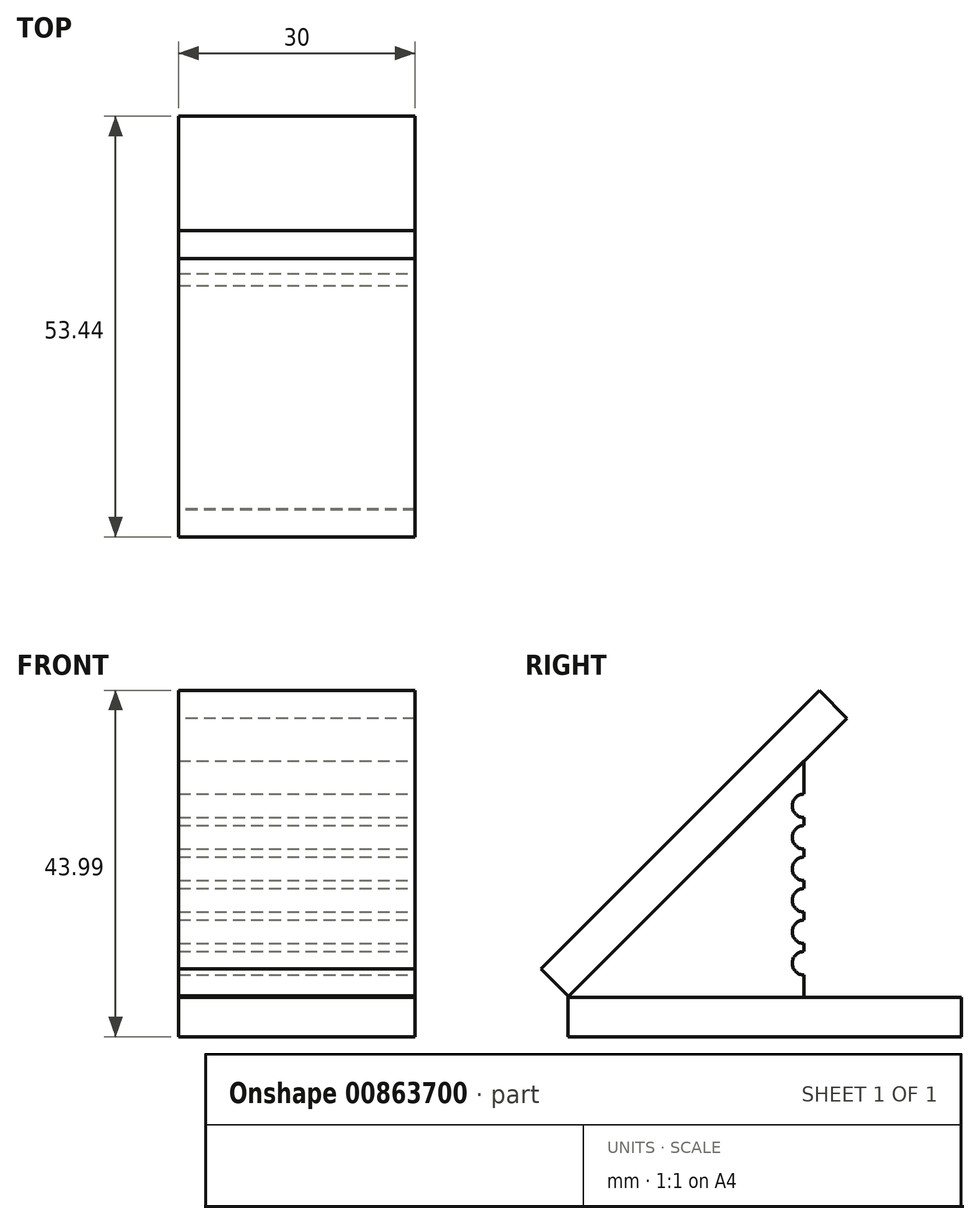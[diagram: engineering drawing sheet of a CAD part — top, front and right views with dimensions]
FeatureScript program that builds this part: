
annotation { "Feature Type Name" : "Feature", "Feature Type Description" : "" }
export const myFeature = defineFeature(function(context is Context, id is Id, definition is map)
    precondition{}
    {
        {
            var Q0;
            Q0=qCreatedBy(makeId("Top.planeOp"),FACE);
            var sketch = newSketch(context, id + "F0", { "sketchPlane" : qUnion([Q0])});
            skLineSegment(sketch, "E0.bottom", {"start": v(-15, 25) * mm, "end": v(15, 25) * mm});
            skLineSegment(sketch, "E0.top", {"start": v(-15, -25) * mm, "end": v(15, -25) * mm});
            skLineSegment(sketch, "E0.left", {"start": v(-15, 25) * mm, "end": v(-15, -25) * mm});
            skLineSegment(sketch, "E0.right", {"start": v(15, 25) * mm, "end": v(15, -25) * mm});
            skSolve(sketch);
        }
        {
            var Q0;
            Q0=makeQuery(id+"F0.imprint","IMPRINT",FACE,{"disambiguationData":[TD([[makeQuery(id+"F0.imprint","IMPRINT",EDGE,{"derivedFrom":sQuery(id+"F0.wireOp",EDGE,"E0.bottom")}),-1.0]])]});
            extrude(context, id + "F1", {"entities" : qUnion([Q0]), "depth" : 5 * mm, "offsetDistance" : 25 * mm});
        }
        {
            var Q0;
            Q0=makeQuery(id+"F1.opExtrude","CAP_EDGE",EDGE,{"disambiguationData":[OSD([sQuery(id+"F0.wireOp",EDGE,"E0.top")])],"isStart":false});
            cPlane(context, id + "F2", {"entities" : qUnion([Q0]), "cplaneType" : CPlaneType.LINE_ANGLE, "offset" : 25 * mm, "angle" : 45 * degree, "oppositeDirection" : true, "width" : 150 * mm, "height" : 150 * mm});
        }
        {
            var Q0;
            Q0=qCreatedBy(id+"F2.planeOp",FACE);
            var sketch = newSketch(context, id + "F3", { "sketchPlane" : qUnion([Q0])});
            skLineSegment(sketch, "E1.bottom", {"start": v(-15, -14) * mm, "end": v(15, -14) * mm});
            skLineSegment(sketch, "E1.top", {"start": v(-15, 36) * mm, "end": v(15, 36) * mm});
            skLineSegment(sketch, "E1.left", {"start": v(-15, -14) * mm, "end": v(-15, 36) * mm});
            skLineSegment(sketch, "E1.right", {"start": v(15, -14) * mm, "end": v(15, 36) * mm});
            skSolve(sketch);
        }
        {
            var Q0;
            Q0=makeQuery(id+"F3.imprint","IMPRINT",FACE,{"disambiguationData":[TD([[makeQuery(id+"F3.imprint","IMPRINT",EDGE,{"derivedFrom":sQuery(id+"F3.wireOp",EDGE,"E1.bottom")}),1.0]])]});
            extrude(context, id + "F4", {"entities" : qUnion([Q0]), "oppositeDirection" : true, "depth" : 5 * mm, "offsetDistance" : 25 * mm});
        }
        {
            var Q0;
            Q0=makeQuery(id+"F1.opExtrude","CAP_FACE",FACE,{"disambiguationData":[OSD([sQuery(id+"F0.wireOp",EDGE,"E0.bottom"),sQuery(id+"F0.wireOp",EDGE,"E0.top"),sQuery(id+"F0.wireOp",EDGE,"E0.left"),sQuery(id+"F0.wireOp",EDGE,"E0.right")])],"isStart":false});
            var sketch = newSketch(context, id + "F5", { "sketchPlane" : qUnion([Q0])});
            skLineSegment(sketch, "E2.top", {"start": v(15, 5) * mm, "end": v(-15, 5) * mm});
            skLineSegment(sketch, "E2.left", {"start": v(15, -25) * mm, "end": v(15, 5) * mm});
            skLineSegment(sketch, "E2.right", {"start": v(-15, -25) * mm, "end": v(-15, 5) * mm});
            skSolve(sketch);
        }
        {
            var Q0;
            Q0=makeQuery(id+"F5.imprint","IMPRINT",FACE,{"disambiguationData":[TD([[makeQuery(id+"F5.imprint","IMPRINT",EDGE,{"derivedFrom":sQuery(id+"F5.wireOp",EDGE,"E2.top")}),1.0]])]});
            extrude(context, id + "F6", {"entities" : qUnion([Q0]), "endBound" : BoundingType.UP_TO_NEXT, "depth" : 25 * mm, "offsetDistance" : 25 * mm});
        }
        {
            var Q0;
            Q0=makeQuery(id+"F6.opExtrude","SWEPT_FACE",FACE,{"disambiguationData":[OSD([sQuery(id+"F5.wireOp",EDGE,"E2.left")])]});
            var sketch = newSketch(context, id + "F7", { "sketchPlane" : qUnion([Q0])});
            skCircle(sketch, "E3", {"center": v(5, 29.32) * mm, "radius": 1.5 * mm});
            skCircle(sketch, "E4.0.1.0", {"center": v(5, 25.32) * mm, "radius": 1.5 * mm});
            skCircle(sketch, "E4.0.2.0", {"center": v(5, 21.32) * mm, "radius": 1.5 * mm});
            skCircle(sketch, "E4.0.3.0", {"center": v(5, 17.32) * mm, "radius": 1.5 * mm});
            skCircle(sketch, "E4.0.4.0", {"center": v(5, 13.32) * mm, "radius": 1.5 * mm});
            skLineSegment(sketch, "E4.direction1", {"start": v(5, 29.32) * mm, "end": v(-20, 29.32) * mm, "construction": true});
            skLineSegment(sketch, "E4.direction2", {"start": v(5, 29.32) * mm, "end": v(5, 25.32) * mm, "construction": true});
            skCircle(sketch, "E5.0.0.5", {"center": v(5, 9.32) * mm, "radius": 1.5 * mm});
            skSolve(sketch);
        }
        {
            var Q0;
            {var subQ0=sQuery(id+"F7.wireOp",EDGE,"E4.0.1.0");var subQ1=makeQuery(id+"F6.opExtrude","SWEPT_EDGE",EDGE,{"disambiguationData":[OSD([sQuery(id+"F0.wireOp",EDGE,"E0.right"),sQuery(id+"F5.wireOp",EDGE,"E2.top"),sQuery(id+"F5.wireOp",EDGE,"E2.left")])]});var subQ2=makeQuery(id+"F7.imprint","INTERSECT",VERTEX,{"disambiguationData":[OD(0.0)],"derivedFrom":[subQ1,subQ0]});Q0=makeQuery(id+"F7.imprint","IMPRINT",FACE,{"disambiguationData":[TD([[makeQuery(id+"F7.imprint","IMPRINT",EDGE,{"disambiguationData":[TD([[subQ2,-1.0]])],"derivedFrom":subQ0}),1.0]])]});}
            var Q1;
            {var subQ0=sQuery(id+"F7.wireOp",EDGE,"E4.0.2.0");var subQ1=makeQuery(id+"F6.opExtrude","SWEPT_EDGE",EDGE,{"disambiguationData":[OSD([sQuery(id+"F0.wireOp",EDGE,"E0.right"),sQuery(id+"F5.wireOp",EDGE,"E2.top"),sQuery(id+"F5.wireOp",EDGE,"E2.left")])]});var subQ2=makeQuery(id+"F7.imprint","INTERSECT",VERTEX,{"disambiguationData":[OD(0.0)],"derivedFrom":[subQ1,subQ0]});Q1=makeQuery(id+"F7.imprint","IMPRINT",FACE,{"disambiguationData":[TD([[makeQuery(id+"F7.imprint","IMPRINT",EDGE,{"disambiguationData":[TD([[subQ2,-1.0]])],"derivedFrom":subQ0}),1.0]])]});}
            var Q2;
            {var subQ0=sQuery(id+"F7.wireOp",EDGE,"E4.0.3.0");var subQ1=makeQuery(id+"F6.opExtrude","SWEPT_EDGE",EDGE,{"disambiguationData":[OSD([sQuery(id+"F0.wireOp",EDGE,"E0.right"),sQuery(id+"F5.wireOp",EDGE,"E2.top"),sQuery(id+"F5.wireOp",EDGE,"E2.left")])]});var subQ2=makeQuery(id+"F7.imprint","INTERSECT",VERTEX,{"disambiguationData":[OD(0.0)],"derivedFrom":[subQ1,subQ0]});Q2=makeQuery(id+"F7.imprint","IMPRINT",FACE,{"disambiguationData":[TD([[makeQuery(id+"F7.imprint","IMPRINT",EDGE,{"disambiguationData":[TD([[subQ2,1.0]])],"derivedFrom":subQ0}),1.0]])]});}
            var Q3;
            {var subQ0=sQuery(id+"F7.wireOp",EDGE,"E4.0.4.0");var subQ1=makeQuery(id+"F6.opExtrude","SWEPT_EDGE",EDGE,{"disambiguationData":[OSD([sQuery(id+"F0.wireOp",EDGE,"E0.right"),sQuery(id+"F5.wireOp",EDGE,"E2.top"),sQuery(id+"F5.wireOp",EDGE,"E2.left")])]});var subQ2=makeQuery(id+"F7.imprint","INTERSECT",VERTEX,{"disambiguationData":[OD(0.0)],"derivedFrom":[subQ1,subQ0]});Q3=makeQuery(id+"F7.imprint","IMPRINT",FACE,{"disambiguationData":[TD([[makeQuery(id+"F7.imprint","IMPRINT",EDGE,{"disambiguationData":[TD([[subQ2,1.0]])],"derivedFrom":subQ0}),1.0]])]});}
            var Q4;
            {var subQ0=sQuery(id+"F7.wireOp",EDGE,"E3");var subQ1=makeQuery(id+"F6.opExtrude","SWEPT_EDGE",EDGE,{"disambiguationData":[OSD([sQuery(id+"F0.wireOp",EDGE,"E0.right"),sQuery(id+"F5.wireOp",EDGE,"E2.top"),sQuery(id+"F5.wireOp",EDGE,"E2.left")])]});var subQ2=makeQuery(id+"F7.imprint","INTERSECT",VERTEX,{"disambiguationData":[OD(0.0)],"derivedFrom":[subQ1,subQ0]});Q4=makeQuery(id+"F7.imprint","IMPRINT",FACE,{"disambiguationData":[TD([[makeQuery(id+"F7.imprint","IMPRINT",EDGE,{"disambiguationData":[TD([[subQ2,-1.0]])],"derivedFrom":subQ0}),1.0]])]});}
            extrude(context, id + "F8", {"entities" : qUnion([Q0, Q1, Q2, Q3, Q4]), "operationType" : NewBodyOperationType.REMOVE, "endBound" : BoundingType.UP_TO_NEXT, "oppositeDirection" : true, "depth" : 25 * mm, "offsetDistance" : 25 * mm});
        }
        {
            var Q0;
            {var subQ0=sQuery(id+"F7.wireOp",EDGE,"E5.0.0.5");var subQ1=makeQuery(id+"F6.opExtrude","SWEPT_EDGE",EDGE,{"disambiguationData":[OSD([sQuery(id+"F0.wireOp",EDGE,"E0.right"),sQuery(id+"F5.wireOp",EDGE,"E2.top"),sQuery(id+"F5.wireOp",EDGE,"E2.left")])]});var subQ2=makeQuery(id+"F7.imprint","INTERSECT",VERTEX,{"disambiguationData":[OD(0.0)],"derivedFrom":[subQ1,subQ0]});Q0=makeQuery(id+"F7.imprint","IMPRINT",FACE,{"disambiguationData":[TD([[makeQuery(id+"F7.imprint","IMPRINT",EDGE,{"disambiguationData":[TD([[subQ2,1.0]])],"derivedFrom":subQ0}),1.0]])]});}
            extrude(context, id + "F9", {"entities" : qUnion([Q0]), "operationType" : NewBodyOperationType.REMOVE, "endBound" : BoundingType.UP_TO_NEXT, "oppositeDirection" : true, "depth" : 25 * mm, "offsetDistance" : 25 * mm});
        }
    });
